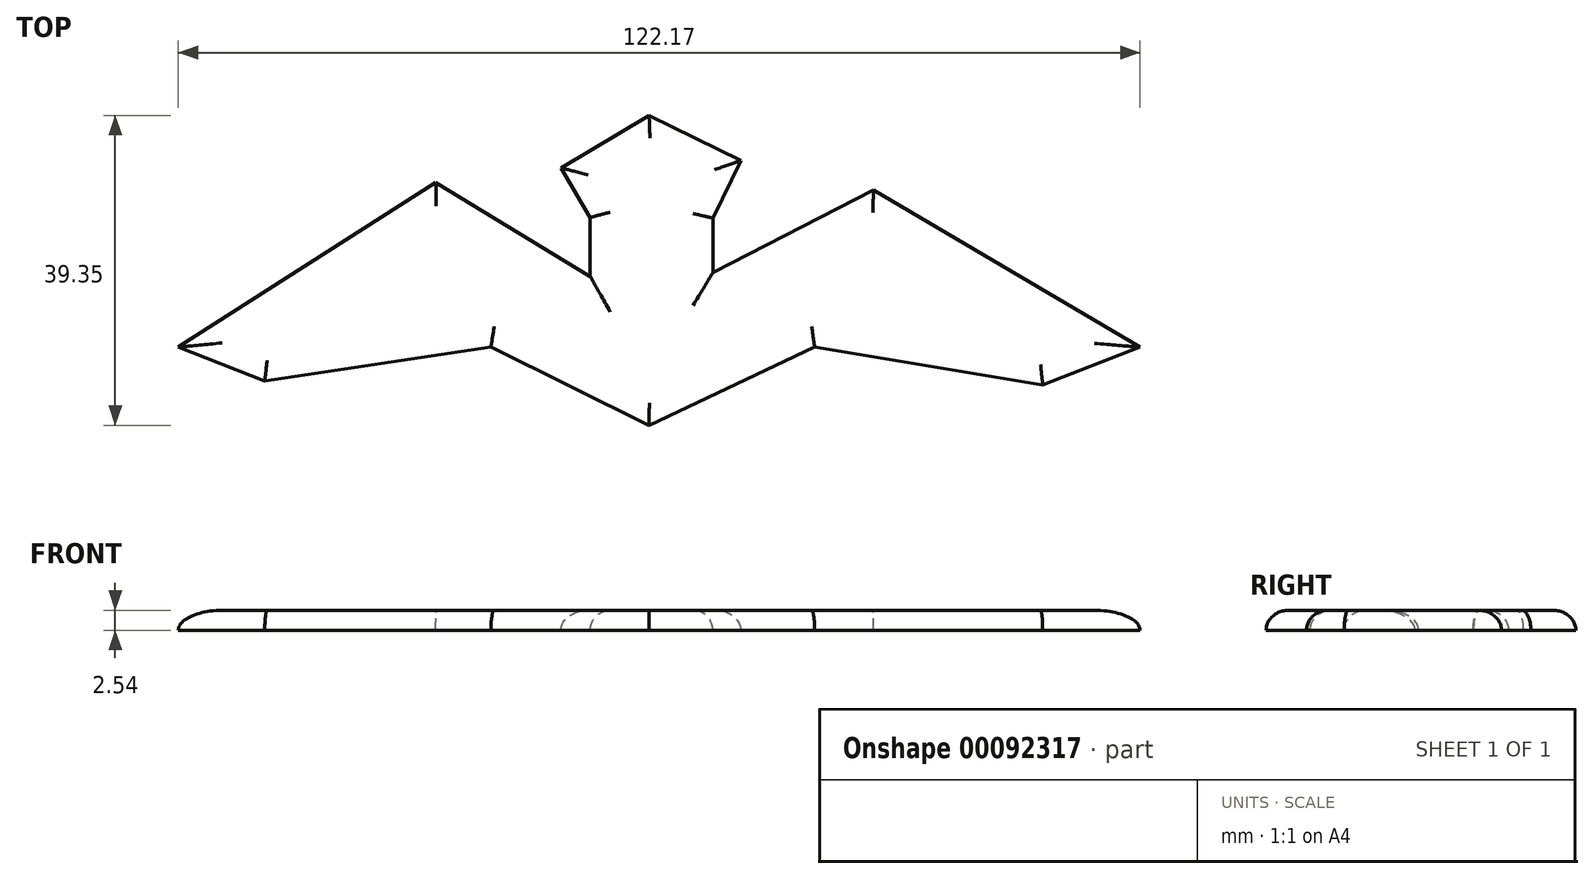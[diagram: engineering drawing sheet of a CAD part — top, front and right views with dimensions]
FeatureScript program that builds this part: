
annotation { "Feature Type Name" : "Feature", "Feature Type Description" : "" }
export const myFeature = defineFeature(function(context is Context, id is Id, definition is map)
    precondition{}
    {
        {
            var Q0;
            Q0=qCreatedBy(makeId("Top.planeOp"),FACE);
            var sketch = newSketch(context, id + "F0", { "sketchPlane" : qUnion([Q0])});
            skLineSegment(sketch, "E0", {"start": v(-59.8, 0) * mm, "end": v(-27.1, 20.9) * mm});
            skLineSegment(sketch, "E1", {"start": v(-27.1, 20.9) * mm, "end": v(-7.48, 9) * mm});
            skLineSegment(sketch, "E2", {"start": v(-7.48, 9) * mm, "end": v(-7.48, 16.47) * mm});
            skLineSegment(sketch, "E3", {"start": v(-7.48, 16.47) * mm, "end": v(-11.21, 22.78) * mm});
            skLineSegment(sketch, "E4", {"start": v(-11.21, 22.78) * mm, "end": v(0, 29.42) * mm});
            skLineSegment(sketch, "E5", {"start": v(0, 29.42) * mm, "end": v(11.68, 23.71) * mm});
            skLineSegment(sketch, "E6", {"start": v(11.68, 23.71) * mm, "end": v(8.1, 16.4) * mm});
            skLineSegment(sketch, "E7", {"start": v(8.1, 16.4) * mm, "end": v(8.1, 9.46) * mm});
            skLineSegment(sketch, "E8", {"start": v(8.1, 9.46) * mm, "end": v(28.5, 19.97) * mm});
            skLineSegment(sketch, "E9", {"start": v(28.5, 19.97) * mm, "end": v(62.37, 0) * mm});
            skLineSegment(sketch, "E10", {"start": v(62.37, 0) * mm, "end": v(50, -4.79) * mm});
            skLineSegment(sketch, "E11", {"start": v(50, -4.79) * mm, "end": v(21.02, 0) * mm});
            skLineSegment(sketch, "E12", {"start": v(21.02, 0) * mm, "end": v(0, -9.93) * mm});
            skLineSegment(sketch, "E13", {"start": v(0, -9.93) * mm, "end": v(-20.1, 0) * mm});
            skLineSegment(sketch, "E14", {"start": v(-20.1, 0) * mm, "end": v(-48.82, -4.32) * mm});
            skLineSegment(sketch, "E15", {"start": v(-48.82, -4.32) * mm, "end": v(-59.8, 0) * mm});
            skSolve(sketch);
        }
        {
            var Q0;
            Q0 = qSketchRegion(id + "F0", true);
            extrude(context, id + "F1", {"entities" : qUnion([Q0]), "depth" : 2.54 * mm});
        }
        {
            var Q0;
            Q0=makeQuery(id+"F1.opExtrude","CAP_EDGE",EDGE,{"disambiguationData":[OSD([sQuery(id+"F0.wireOp",EDGE,"E0")])],"isStart":false});
            var Q1;
            Q1=makeQuery(id+"F1.opExtrude","CAP_EDGE",EDGE,{"disambiguationData":[OSD([sQuery(id+"F0.wireOp",EDGE,"E1")])],"isStart":false});
            var Q2;
            Q2=makeQuery(id+"F1.opExtrude","CAP_EDGE",EDGE,{"disambiguationData":[OSD([sQuery(id+"F0.wireOp",EDGE,"E2")])],"isStart":false});
            var Q3;
            Q3=makeQuery(id+"F1.opExtrude","CAP_EDGE",EDGE,{"disambiguationData":[OSD([sQuery(id+"F0.wireOp",EDGE,"E3")])],"isStart":false});
            var Q4;
            Q4=makeQuery(id+"F1.opExtrude","CAP_EDGE",EDGE,{"disambiguationData":[OSD([sQuery(id+"F0.wireOp",EDGE,"E4")])],"isStart":false});
            var Q5;
            Q5=makeQuery(id+"F1.opExtrude","CAP_EDGE",EDGE,{"disambiguationData":[OSD([sQuery(id+"F0.wireOp",EDGE,"E5")])],"isStart":false});
            var Q6;
            Q6=makeQuery(id+"F1.opExtrude","CAP_EDGE",EDGE,{"disambiguationData":[OSD([sQuery(id+"F0.wireOp",EDGE,"E6")])],"isStart":false});
            var Q7;
            Q7=makeQuery(id+"F1.opExtrude","CAP_EDGE",EDGE,{"disambiguationData":[OSD([sQuery(id+"F0.wireOp",EDGE,"E7")])],"isStart":false});
            var Q8;
            Q8=makeQuery(id+"F1.opExtrude","CAP_EDGE",EDGE,{"disambiguationData":[OSD([sQuery(id+"F0.wireOp",EDGE,"E8")])],"isStart":false});
            var Q9;
            Q9=makeQuery(id+"F1.opExtrude","CAP_EDGE",EDGE,{"disambiguationData":[OSD([sQuery(id+"F0.wireOp",EDGE,"E9")])],"isStart":false});
            var Q10;
            Q10=makeQuery(id+"F1.opExtrude","CAP_FACE",FACE,{"disambiguationData":[OSD([sQuery(id+"F0.wireOp",EDGE,"E0"),sQuery(id+"F0.wireOp",EDGE,"E1"),sQuery(id+"F0.wireOp",EDGE,"E2"),sQuery(id+"F0.wireOp",EDGE,"E3"),sQuery(id+"F0.wireOp",EDGE,"E4"),sQuery(id+"F0.wireOp",EDGE,"E5"),sQuery(id+"F0.wireOp",EDGE,"E6"),sQuery(id+"F0.wireOp",EDGE,"E7"),sQuery(id+"F0.wireOp",EDGE,"E8"),sQuery(id+"F0.wireOp",EDGE,"E9"),sQuery(id+"F0.wireOp",EDGE,"E10"),sQuery(id+"F0.wireOp",EDGE,"E11"),sQuery(id+"F0.wireOp",EDGE,"E12"),sQuery(id+"F0.wireOp",EDGE,"E13"),sQuery(id+"F0.wireOp",EDGE,"E14"),sQuery(id+"F0.wireOp",EDGE,"E15")])],"isStart":false});
            fillet(context, id + "F2", {"entities" : qUnion([Q0, Q1, Q2, Q3, Q4, Q5, Q6, Q7, Q8, Q9, Q10]), "radius" : 2.54 * mm, "tangentPropagation" : true, "allowEdgeOverflow" : false});
        }
    });
